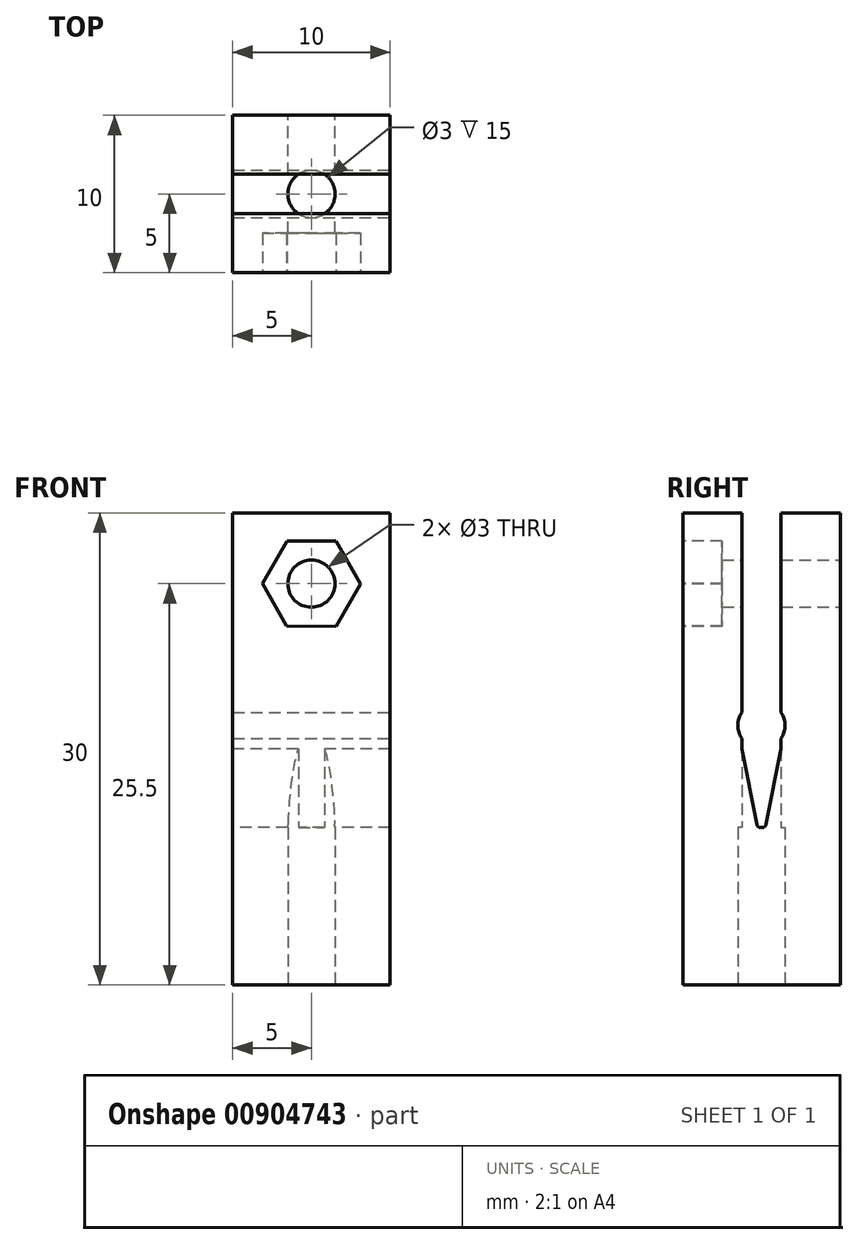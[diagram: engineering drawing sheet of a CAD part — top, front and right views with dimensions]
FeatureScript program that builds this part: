
annotation { "Feature Type Name" : "Feature", "Feature Type Description" : "" }
export const myFeature = defineFeature(function(context is Context, id is Id, definition is map)
    precondition{}
    {
        {
            var Q0;
            Q0=qCreatedBy(makeId("Top.planeOp"),FACE);
            var sketch = newSketch(context, id + "F0", { "sketchPlane" : qUnion([Q0])});
            skLineSegment(sketch, "E0.bottom", {"start": v(5, -5) * mm, "end": v(-5, -5) * mm});
            skLineSegment(sketch, "E0.top", {"start": v(5, 5) * mm, "end": v(-5, 5) * mm});
            skLineSegment(sketch, "E0.left", {"start": v(5, -5) * mm, "end": v(5, 5) * mm});
            skLineSegment(sketch, "E0.right", {"start": v(-5, -5) * mm, "end": v(-5, 5) * mm});
            skPoint(sketch, "E0.middle", {"position": v(0, 0) * mm});
            skSolve(sketch);
        }
        {
            var Q0;
            Q0 = qSketchRegion(id + "F0", true);
            extrude(context, id + "F1", {"entities" : qUnion([Q0]), "depth" : 30 * mm, "offsetDistance" : 25 * mm});
        }
        {
            var Q0;
            Q0=makeQuery(id+"F1.opExtrude","CAP_FACE",FACE,{"disambiguationData":[OSD([sQuery(id+"F0.wireOp",EDGE,"E0.bottom"),sQuery(id+"F0.wireOp",EDGE,"E0.top"),sQuery(id+"F0.wireOp",EDGE,"E0.left"),sQuery(id+"F0.wireOp",EDGE,"E0.right")])],"isStart":true});
            var sketch = newSketch(context, id + "F2", { "sketchPlane" : qUnion([Q0])});
            skCircle(sketch, "E1", {"center": v(0, 0) * mm, "radius": 1.5 * mm});
            skSolve(sketch);
        }
        {
            var Q0;
            Q0 = qSketchRegion(id + "F2", true);
            extrude(context, id + "F3", {"entities" : qUnion([Q0]), "operationType" : NewBodyOperationType.REMOVE, "oppositeDirection" : true, "depth" : 10 * mm, "offsetDistance" : 25 * mm});
        }
        {
            var Q0;
            Q0=makeQuery(id+"F1.opExtrude","SWEPT_FACE",FACE,{"disambiguationData":[OSD([sQuery(id+"F0.wireOp",EDGE,"E0.left")])]});
            var sketch = newSketch(context, id + "F4", { "sketchPlane" : qUnion([Q0])});
            skCircle(sketch, "E2", {"center": v(0, 16.5) * mm, "radius": 1.5 * mm});
            skPoint(sketch, "E3.middle", {"position": v(0, 30) * mm});
            skLineSegment(sketch, "E4.bottom", {"start": v(1.25, 10) * mm, "end": v(-1.25, 10) * mm});
            skLineSegment(sketch, "E4.top", {"start": v(1.25, 30) * mm, "end": v(-1.25, 30) * mm});
            skLineSegment(sketch, "E4.left", {"start": v(1.25, 10) * mm, "end": v(1.25, 30) * mm});
            skLineSegment(sketch, "E4.right", {"start": v(-1.25, 10) * mm, "end": v(-1.25, 30) * mm});
            skPoint(sketch, "E4.middle", {"position": v(0, 20) * mm});
            skSolve(sketch);
        }
        {
            var Q0;
            Q0 = qSketchRegion(id + "F4", true);
            extrude(context, id + "F5", {"entities" : qUnion([Q0]), "operationType" : NewBodyOperationType.REMOVE, "oppositeDirection" : true, "depth" : 25 * mm, "offsetDistance" : 25 * mm});
        }
        {
            var Q0;
            {var subQ0=sQuery(id+"F4.wireOp",EDGE,"E4.bottom");var subQ1=makeQuery(id+"F5.opExtrude","SWEPT_FACE",FACE,{"disambiguationData":[OSD([subQ0])]});var subQ3=sQuery(id+"F4.wireOp",EDGE,"E4.left");var subQ4=makeQuery(id+"F5.opExtrude","SWEPT_FACE",FACE,{"disambiguationData":[OSD([subQ3]),TDD([makeQuery(id+"F4.imprint","IMPRINT",EDGE,{"disambiguationData":[TD([[makeQuery(id+"F4.imprint","INTERSECT",VERTEX,{"derivedFrom":[subQ0,subQ3]}),-1.0]])],"derivedFrom":subQ3})])]});Q0=makeQuery(id+"F5.boolean.opBoolean","COPY",EDGE,{"disambiguationData":[topologyDisambiguationEdgeConnected([subQ1,subQ4]),TD([makeQuery(id+"F1.opExtrude","SWEPT_FACE",FACE,{"disambiguationData":[OSD([sQuery(id+"F0.wireOp",EDGE,"E0.right")])]})])],"derivedFrom":makeQuery(id+"F5.opExtrude","SWEPT_EDGE",EDGE,{"disambiguationData":[OSD([subQ0,subQ3])]})});}
            var Q1;
            {var subQ0=sQuery(id+"F4.wireOp",EDGE,"E4.bottom");var subQ1=makeQuery(id+"F5.opExtrude","SWEPT_FACE",FACE,{"disambiguationData":[OSD([subQ0])]});var subQ3=sQuery(id+"F4.wireOp",EDGE,"E4.right");var subQ4=makeQuery(id+"F5.opExtrude","SWEPT_FACE",FACE,{"disambiguationData":[OSD([subQ3]),TDD([makeQuery(id+"F4.imprint","IMPRINT",EDGE,{"disambiguationData":[TD([[makeQuery(id+"F4.imprint","INTERSECT",VERTEX,{"derivedFrom":[subQ0,subQ3]}),-1.0]])],"derivedFrom":subQ3})])]});Q1=makeQuery(id+"F5.boolean.opBoolean","COPY",EDGE,{"disambiguationData":[topologyDisambiguationEdgeConnected([subQ1,subQ4]),TD([makeQuery(id+"F1.opExtrude","SWEPT_FACE",FACE,{"disambiguationData":[OSD([sQuery(id+"F0.wireOp",EDGE,"E0.right")])]})])],"derivedFrom":makeQuery(id+"F5.opExtrude","SWEPT_EDGE",EDGE,{"disambiguationData":[OSD([subQ0,subQ3])]})});}
            var Q2;
            {var subQ0=sQuery(id+"F4.wireOp",EDGE,"E4.bottom");var subQ1=makeQuery(id+"F5.opExtrude","SWEPT_FACE",FACE,{"disambiguationData":[OSD([subQ0])]});var subQ3=sQuery(id+"F4.wireOp",EDGE,"E4.left");var subQ4=makeQuery(id+"F5.opExtrude","SWEPT_FACE",FACE,{"disambiguationData":[OSD([subQ3]),TDD([makeQuery(id+"F4.imprint","IMPRINT",EDGE,{"disambiguationData":[TD([[makeQuery(id+"F4.imprint","INTERSECT",VERTEX,{"derivedFrom":[subQ0,subQ3]}),-1.0]])],"derivedFrom":subQ3})])]});Q2=makeQuery(id+"F5.boolean.opBoolean","COPY",EDGE,{"disambiguationData":[topologyDisambiguationEdgeConnected([subQ1,subQ4]),TD([makeQuery(id+"F1.opExtrude","SWEPT_FACE",FACE,{"disambiguationData":[OSD([sQuery(id+"F0.wireOp",EDGE,"E0.left")])]})])],"derivedFrom":makeQuery(id+"F5.opExtrude","SWEPT_EDGE",EDGE,{"disambiguationData":[OSD([subQ0,subQ3])]})});}
            chamfer(context, id + "F6", {"entities" : qUnion([Q0, Q1, Q2]), "chamferType" : ChamferType.TWO_OFFSETS, "width1" : 5 * mm, "oppositeDirection" : false, "width2" : 1 * mm, "tangentPropagation" : true});
        }
        {
            var Q0;
            {var subQ0=sQuery(id+"F4.wireOp",EDGE,"E4.bottom");var subQ1=makeQuery(id+"F5.opExtrude","SWEPT_FACE",FACE,{"disambiguationData":[OSD([subQ0])]});var subQ3=sQuery(id+"F4.wireOp",EDGE,"E4.right");var subQ4=makeQuery(id+"F5.opExtrude","SWEPT_FACE",FACE,{"disambiguationData":[OSD([subQ3]),TDD([makeQuery(id+"F4.imprint","IMPRINT",EDGE,{"disambiguationData":[TD([[makeQuery(id+"F4.imprint","INTERSECT",VERTEX,{"derivedFrom":[subQ0,subQ3]}),-1.0]])],"derivedFrom":subQ3})])]});Q0=makeQuery(id+"F5.boolean.opBoolean","COPY",EDGE,{"disambiguationData":[topologyDisambiguationEdgeConnected([subQ1,subQ4]),TD([makeQuery(id+"F1.opExtrude","SWEPT_FACE",FACE,{"disambiguationData":[OSD([sQuery(id+"F0.wireOp",EDGE,"E0.left")])]})])],"derivedFrom":makeQuery(id+"F5.opExtrude","SWEPT_EDGE",EDGE,{"disambiguationData":[OSD([subQ0,subQ3])]})});}
            chamfer(context, id + "F7", {"entities" : qUnion([Q0]), "chamferType" : ChamferType.TWO_OFFSETS, "width1" : 1 * mm, "oppositeDirection" : false, "width2" : 5 * mm, "tangentPropagation" : true});
        }
        {
            var Q0;
            {var subQ0=sQuery(id+"F4.wireOp",EDGE,"E4.left");var subQ1=sQuery(id+"F4.wireOp",EDGE,"E4.bottom");var subQ3=makeQuery(id+"F5.opExtrude","SWEPT_FACE",FACE,{"disambiguationData":[OSD([subQ0]),TDD([makeQuery(id+"F4.imprint","IMPRINT",EDGE,{"disambiguationData":[TD([[makeQuery(id+"F4.imprint","INTERSECT",VERTEX,{"derivedFrom":[subQ1,subQ0]}),-1.0]])],"derivedFrom":subQ0})])]});var subQ6=makeQuery(id+"F1.opExtrude","SWEPT_FACE",FACE,{"disambiguationData":[OSD([sQuery(id+"F0.wireOp",EDGE,"E0.right")])]});var subQ9=makeQuery(id+"F5.opExtrude","SWEPT_FACE",FACE,{"disambiguationData":[OSD([subQ1])]});Q0=makeQuery(id+"F6.opChamfer","BLEND_EDGE",EDGE,{"blendedFrom":[makeQuery(id+"F5.boolean.opBoolean","COPY",EDGE,{"disambiguationData":[topologyDisambiguationEdgeConnected([subQ9,subQ3]),TD([subQ6])],"derivedFrom":makeQuery(id+"F5.opExtrude","SWEPT_EDGE",EDGE,{"disambiguationData":[OSD([subQ1,subQ0])]})}),makeQuery(id+"F5.boolean.opBoolean","COPY",FACE,{"disambiguationData":[TD([subQ6])],"derivedFrom":subQ9})],"blendedInto":[makeQuery(id+"F5.boolean.opBoolean","COPY",FACE,{"disambiguationData":[TD([subQ6])],"derivedFrom":subQ9})]});}
            var Q1;
            {var subQ1=sQuery(id+"F4.wireOp",EDGE,"E4.bottom");var subQ5=makeQuery(id+"F1.opExtrude","SWEPT_FACE",FACE,{"disambiguationData":[OSD([sQuery(id+"F0.wireOp",EDGE,"E0.right")])]});var subQ7=sQuery(id+"F4.wireOp",EDGE,"E4.right");var subQ8=makeQuery(id+"F5.opExtrude","SWEPT_FACE",FACE,{"disambiguationData":[OSD([subQ7]),TDD([makeQuery(id+"F4.imprint","IMPRINT",EDGE,{"disambiguationData":[TD([[makeQuery(id+"F4.imprint","INTERSECT",VERTEX,{"derivedFrom":[subQ1,subQ7]}),-1.0]])],"derivedFrom":subQ7})])]});var subQ9=makeQuery(id+"F5.opExtrude","SWEPT_FACE",FACE,{"disambiguationData":[OSD([subQ1])]});Q1=makeQuery(id+"F6.opChamfer","BLEND_EDGE",EDGE,{"blendedFrom":[makeQuery(id+"F5.boolean.opBoolean","COPY",EDGE,{"disambiguationData":[topologyDisambiguationEdgeConnected([subQ9,subQ8]),TD([subQ5])],"derivedFrom":makeQuery(id+"F5.opExtrude","SWEPT_EDGE",EDGE,{"disambiguationData":[OSD([subQ1,subQ7])]})}),makeQuery(id+"F5.boolean.opBoolean","COPY",FACE,{"disambiguationData":[TD([subQ5])],"derivedFrom":subQ9})],"blendedInto":[makeQuery(id+"F5.boolean.opBoolean","COPY",FACE,{"disambiguationData":[TD([subQ5])],"derivedFrom":subQ9})]});}
            var Q2;
            {var subQ0=sQuery(id+"F4.wireOp",EDGE,"E4.left");var subQ1=sQuery(id+"F4.wireOp",EDGE,"E4.bottom");var subQ3=makeQuery(id+"F5.opExtrude","SWEPT_FACE",FACE,{"disambiguationData":[OSD([subQ0]),TDD([makeQuery(id+"F4.imprint","IMPRINT",EDGE,{"disambiguationData":[TD([[makeQuery(id+"F4.imprint","INTERSECT",VERTEX,{"derivedFrom":[subQ1,subQ0]}),-1.0]])],"derivedFrom":subQ0})])]});var subQ7=makeQuery(id+"F1.opExtrude","SWEPT_FACE",FACE,{"disambiguationData":[OSD([sQuery(id+"F0.wireOp",EDGE,"E0.left")])]});var subQ9=makeQuery(id+"F5.opExtrude","SWEPT_FACE",FACE,{"disambiguationData":[OSD([subQ1])]});Q2=makeQuery(id+"F6.opChamfer","BLEND_EDGE",EDGE,{"blendedFrom":[makeQuery(id+"F5.boolean.opBoolean","COPY",EDGE,{"disambiguationData":[topologyDisambiguationEdgeConnected([subQ9,subQ3]),TD([subQ7])],"derivedFrom":makeQuery(id+"F5.opExtrude","SWEPT_EDGE",EDGE,{"disambiguationData":[OSD([subQ1,subQ0])]})}),makeQuery(id+"F5.boolean.opBoolean","COPY",FACE,{"disambiguationData":[TD([subQ7])],"derivedFrom":subQ9})],"blendedInto":[makeQuery(id+"F5.boolean.opBoolean","COPY",FACE,{"disambiguationData":[TD([subQ7])],"derivedFrom":subQ9})]});}
            var Q3;
            {var subQ1=sQuery(id+"F4.wireOp",EDGE,"E4.bottom");var subQ6=makeQuery(id+"F1.opExtrude","SWEPT_FACE",FACE,{"disambiguationData":[OSD([sQuery(id+"F0.wireOp",EDGE,"E0.left")])]});var subQ7=sQuery(id+"F4.wireOp",EDGE,"E4.right");var subQ8=makeQuery(id+"F5.opExtrude","SWEPT_FACE",FACE,{"disambiguationData":[OSD([subQ7]),TDD([makeQuery(id+"F4.imprint","IMPRINT",EDGE,{"disambiguationData":[TD([[makeQuery(id+"F4.imprint","INTERSECT",VERTEX,{"derivedFrom":[subQ1,subQ7]}),-1.0]])],"derivedFrom":subQ7})])]});var subQ9=makeQuery(id+"F5.opExtrude","SWEPT_FACE",FACE,{"disambiguationData":[OSD([subQ1])]});Q3=makeQuery(id+"F7.opChamfer","BLEND_EDGE",EDGE,{"blendedFrom":[makeQuery(id+"F5.boolean.opBoolean","COPY",EDGE,{"disambiguationData":[topologyDisambiguationEdgeConnected([subQ9,subQ8]),TD([subQ6])],"derivedFrom":makeQuery(id+"F5.opExtrude","SWEPT_EDGE",EDGE,{"disambiguationData":[OSD([subQ1,subQ7])]})}),makeQuery(id+"F5.boolean.opBoolean","COPY",FACE,{"disambiguationData":[TD([subQ6])],"derivedFrom":subQ9})],"blendedInto":[makeQuery(id+"F5.boolean.opBoolean","COPY",FACE,{"disambiguationData":[TD([subQ6])],"derivedFrom":subQ9})]});}
            fillet(context, id + "F8", {"entities" : qUnion([Q0, Q1, Q2, Q3]), "radius" : 0.25 * mm, "tangentPropagation" : true, "allowEdgeOverflow" : false});
        }
        {
            var Q0;
            Q0=makeQuery(id+"F1.opExtrude","SWEPT_FACE",FACE,{"disambiguationData":[OSD([sQuery(id+"F0.wireOp",EDGE,"E0.top")])]});
            var sketch = newSketch(context, id + "F9", { "sketchPlane" : qUnion([Q0])});
            skCircle(sketch, "E5", {"center": v(0, 25.5) * mm, "radius": 1.5 * mm});
            skSolve(sketch);
        }
        {
            var Q0;
            Q0 = qSketchRegion(id + "F9", true);
            extrude(context, id + "F10", {"entities" : qUnion([Q0]), "operationType" : NewBodyOperationType.REMOVE, "oppositeDirection" : true, "depth" : 25 * mm, "offsetDistance" : 25 * mm});
        }
        {
            var Q0;
            Q0=makeQuery(id+"F1.opExtrude","SWEPT_FACE",FACE,{"disambiguationData":[OSD([sQuery(id+"F0.wireOp",EDGE,"E0.bottom")])]});
            var sketch = newSketch(context, id + "F11", { "sketchPlane" : qUnion([Q0])});
            skCircle(sketch, "E6.cCircle", {"center": v(0, 25.5) * mm, "radius": 2.7 * mm, "construction": true});
            skLineSegment(sketch, "E6.0", {"start": v(3.12, 25.48) * mm, "end": v(1.54, 22.8) * mm});
            skLineSegment(sketch, "E6.1", {"start": v(1.54, 22.8) * mm, "end": v(-1.57, 22.8) * mm});
            skLineSegment(sketch, "E6.2", {"start": v(-1.57, 22.8) * mm, "end": v(-3.12, 25.52) * mm});
            skLineSegment(sketch, "E6.3", {"start": v(-3.12, 25.52) * mm, "end": v(-1.54, 28.2) * mm});
            skLineSegment(sketch, "E6.4", {"start": v(-1.54, 28.2) * mm, "end": v(1.57, 28.2) * mm});
            skLineSegment(sketch, "E6.5", {"start": v(1.57, 28.2) * mm, "end": v(3.12, 25.48) * mm});
            skPoint(sketch, "E6.0.midPoint", {"position": v(2.33, 24.14) * mm});
            skSolve(sketch);
        }
        {
            var Q0;
            Q0 = qSketchRegion(id + "F11", true);
            extrude(context, id + "F12", {"entities" : qUnion([Q0]), "operationType" : NewBodyOperationType.REMOVE, "oppositeDirection" : true, "depth" : 2.5 * mm, "offsetDistance" : 25 * mm});
        }
    });
